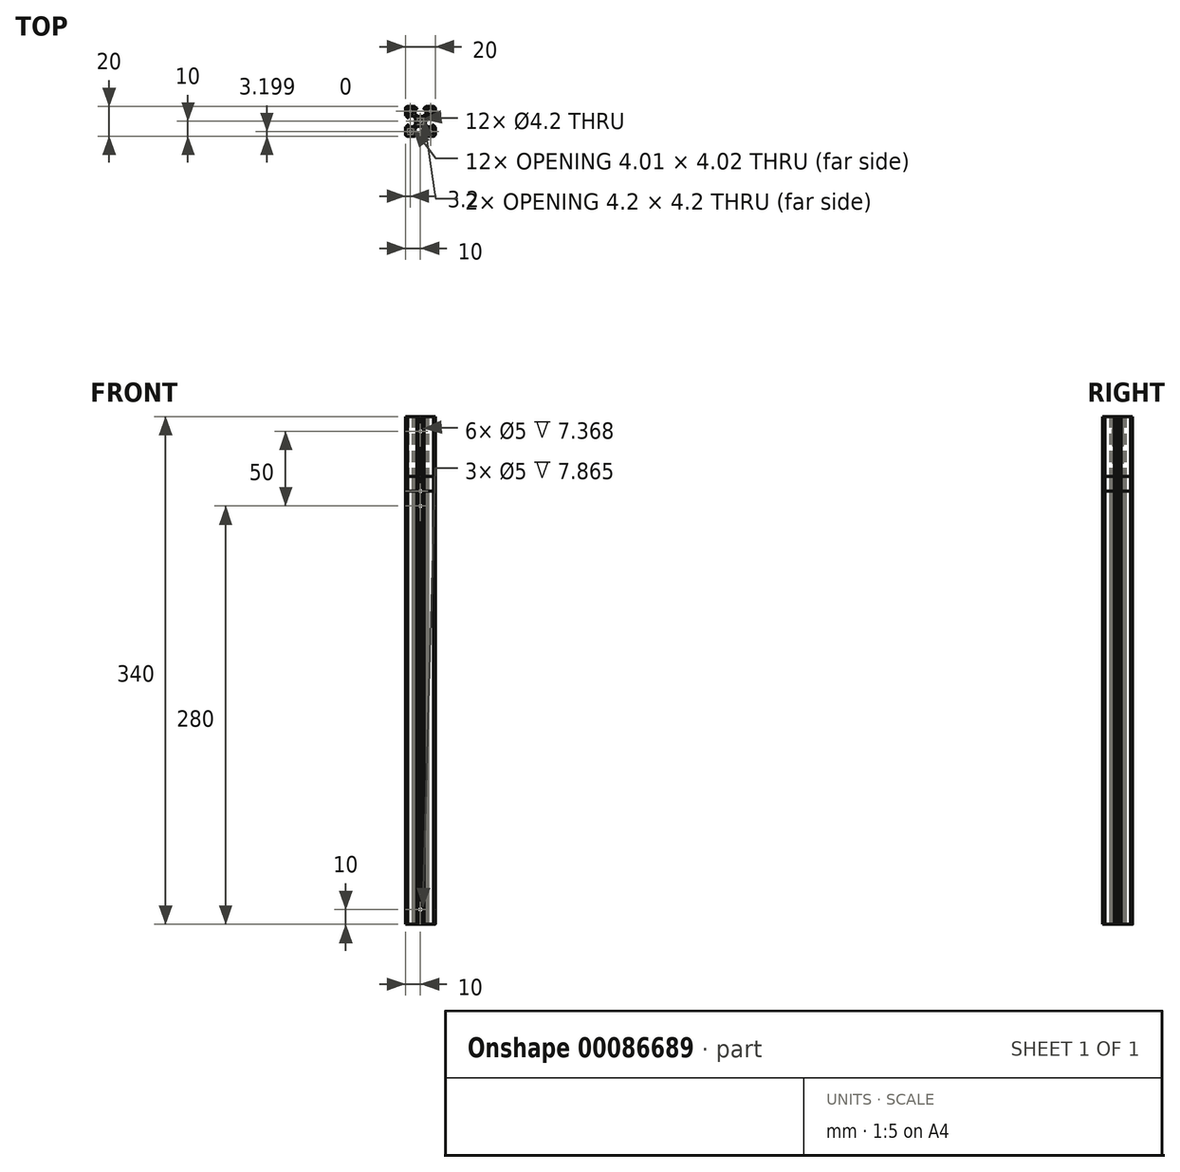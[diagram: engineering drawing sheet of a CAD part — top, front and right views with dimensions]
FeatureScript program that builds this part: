
annotation { "Feature Type Name" : "Feature", "Feature Type Description" : "" }
export const myFeature = defineFeature(function(context is Context, id is Id, definition is map)
    precondition{}
    {
        {
            var Q0;
            Q0=qCreatedBy(makeId("Top.planeOp"),FACE);
            var sketch = newSketch(context, id + "F0", { "sketchPlane" : qUnion([Q0])});
            skCircle(sketch, "E0", {"center": v(0, 0) * mm, "radius": 2.1 * mm});
            skArc(sketch, "E1", {"start": v(-5.39, 4.8) * mm, "mid": v(-4.94, 4.93) * mm, "end": v(-4.8, 5.38) * mm});
            skLineSegment(sketch, "E2", {"start": v(-5.39, 4.8) * mm, "end": v(-8.39, 4.8) * mm});
            skArc(sketch, "E3", {"start": v(-8.8, 5.38) * mm, "mid": v(-8.72, 5) * mm, "end": v(-8.39, 4.8) * mm});
            skLineSegment(sketch, "E4", {"start": v(-8.8, 5.38) * mm, "end": v(-8.8, 8.38) * mm});
            skArc(sketch, "E5", {"start": v(-8.4, 8.8) * mm, "mid": v(-8.67, 8.65) * mm, "end": v(-8.8, 8.38) * mm});
            skLineSegment(sketch, "E6", {"start": v(-8.4, 8.8) * mm, "end": v(-5.4, 8.8) * mm});
            skArc(sketch, "E7", {"start": v(-4.8, 8.38) * mm, "mid": v(-5, 8.72) * mm, "end": v(-5.4, 8.8) * mm});
            skLineSegment(sketch, "E8", {"start": v(-4.8, 8.38) * mm, "end": v(-4.8, 5.38) * mm});
            skArc(sketch, "E9", {"start": v(5.39, -4.8) * mm, "mid": v(4.94, -4.93) * mm, "end": v(4.8, -5.38) * mm});
            skLineSegment(sketch, "E10", {"start": v(5.39, -4.8) * mm, "end": v(8.39, -4.8) * mm});
            skArc(sketch, "E11", {"start": v(8.8, -5.38) * mm, "mid": v(8.72, -5) * mm, "end": v(8.39, -4.8) * mm});
            skLineSegment(sketch, "E12", {"start": v(8.8, -5.38) * mm, "end": v(8.8, -8.38) * mm});
            skArc(sketch, "E13", {"start": v(8.4, -8.8) * mm, "mid": v(8.67, -8.65) * mm, "end": v(8.8, -8.38) * mm});
            skLineSegment(sketch, "E14", {"start": v(8.4, -8.8) * mm, "end": v(5.4, -8.8) * mm});
            skArc(sketch, "E15", {"start": v(4.8, -8.38) * mm, "mid": v(5, -8.72) * mm, "end": v(5.4, -8.8) * mm});
            skLineSegment(sketch, "E16", {"start": v(4.8, -8.38) * mm, "end": v(4.8, -5.38) * mm});
            skLineSegment(sketch, "E17", {"start": v(8.8, 5.38) * mm, "end": v(8.8, 8.38) * mm});
            skArc(sketch, "E18", {"start": v(8.8, 5.38) * mm, "mid": v(8.72, 5) * mm, "end": v(8.39, 4.8) * mm});
            skLineSegment(sketch, "E19", {"start": v(5.39, 4.8) * mm, "end": v(8.39, 4.8) * mm});
            skArc(sketch, "E20", {"start": v(5.39, 4.8) * mm, "mid": v(4.94, 4.93) * mm, "end": v(4.8, 5.38) * mm});
            skLineSegment(sketch, "E21", {"start": v(4.8, 8.38) * mm, "end": v(4.8, 5.38) * mm});
            skArc(sketch, "E22", {"start": v(4.8, 8.38) * mm, "mid": v(5, 8.72) * mm, "end": v(5.4, 8.8) * mm});
            skLineSegment(sketch, "E23", {"start": v(8.4, 8.8) * mm, "end": v(5.4, 8.8) * mm});
            skArc(sketch, "E24", {"start": v(8.4, 8.8) * mm, "mid": v(8.67, 8.65) * mm, "end": v(8.8, 8.38) * mm});
            skLineSegment(sketch, "E25", {"start": v(-8.8, -5.38) * mm, "end": v(-8.8, -8.38) * mm});
            skArc(sketch, "E26", {"start": v(-8.8, -5.38) * mm, "mid": v(-8.72, -5) * mm, "end": v(-8.39, -4.8) * mm});
            skLineSegment(sketch, "E27", {"start": v(-5.39, -4.8) * mm, "end": v(-8.39, -4.8) * mm});
            skArc(sketch, "E28", {"start": v(-5.39, -4.8) * mm, "mid": v(-4.94, -4.93) * mm, "end": v(-4.8, -5.38) * mm});
            skLineSegment(sketch, "E29", {"start": v(-4.8, -8.38) * mm, "end": v(-4.8, -5.38) * mm});
            skArc(sketch, "E30", {"start": v(-4.8, -8.38) * mm, "mid": v(-5, -8.72) * mm, "end": v(-5.4, -8.8) * mm});
            skLineSegment(sketch, "E31", {"start": v(-8.4, -8.8) * mm, "end": v(-5.4, -8.8) * mm});
            skArc(sketch, "E32", {"start": v(-8.4, -8.8) * mm, "mid": v(-8.67, -8.65) * mm, "end": v(-8.8, -8.38) * mm});
            skArc(sketch, "E33", {"start": v(-10, 4.25) * mm, "mid": v(-9.94, 3.95) * mm, "end": v(-9.77, 3.7) * mm});
            skLineSegment(sketch, "E34", {"start": v(-9.77, 3.7) * mm, "end": v(-8.49, 2.4) * mm});
            skArc(sketch, "E35", {"start": v(-8.49, 2.4) * mm, "mid": v(-8.27, 2.36) * mm, "end": v(-8.14, 2.54) * mm});
            skLineSegment(sketch, "E36", {"start": v(-8.14, 2.54) * mm, "end": v(-8.14, 3.6) * mm});
            skLineSegment(sketch, "E37", {"start": v(-8.14, 3.6) * mm, "end": v(-5.03, 3.6) * mm});
            skLineSegment(sketch, "E38", {"start": v(-5.03, 3.6) * mm, "end": v(-3.4, 1.97) * mm});
            skLineSegment(sketch, "E39", {"start": v(-3.4, 1.97) * mm, "end": v(-3.4, 0.38) * mm});
            skLineSegment(sketch, "E40", {"start": v(-3.4, 0.38) * mm, "end": v(-3.02, 0) * mm});
            skLineSegment(sketch, "E41", {"start": v(-3.4, -0.38) * mm, "end": v(-3.02, 0) * mm});
            skLineSegment(sketch, "E42", {"start": v(-3.4, -1.97) * mm, "end": v(-3.4, -0.38) * mm});
            skLineSegment(sketch, "E43", {"start": v(-5.03, -3.6) * mm, "end": v(-3.4, -1.97) * mm});
            skLineSegment(sketch, "E44", {"start": v(-8.14, -3.6) * mm, "end": v(-5.03, -3.6) * mm});
            skLineSegment(sketch, "E45", {"start": v(-8.14, -2.54) * mm, "end": v(-8.14, -3.6) * mm});
            skArc(sketch, "E46", {"start": v(-8.49, -2.4) * mm, "mid": v(-8.27, -2.36) * mm, "end": v(-8.14, -2.54) * mm});
            skLineSegment(sketch, "E47", {"start": v(-9.77, -3.7) * mm, "end": v(-8.49, -2.4) * mm});
            skArc(sketch, "E48", {"start": v(-10, -4.25) * mm, "mid": v(-9.94, -3.95) * mm, "end": v(-9.77, -3.7) * mm});
            skLineSegment(sketch, "E49", {"start": v(-10, -8.58) * mm, "end": v(-10, -4.25) * mm});
            skArc(sketch, "E50", {"start": v(-8.6, -10) * mm, "mid": v(-9.57, -9.56) * mm, "end": v(-10, -8.58) * mm});
            skLineSegment(sketch, "E51", {"start": v(-4.04, -10) * mm, "end": v(-8.6, -10) * mm});
            skArc(sketch, "E52", {"start": v(-3.48, -9.77) * mm, "mid": v(-3.74, -9.94) * mm, "end": v(-4.04, -10) * mm});
            skLineSegment(sketch, "E53", {"start": v(-2.37, -8.66) * mm, "end": v(-3.48, -9.77) * mm});
            skArc(sketch, "E54", {"start": v(-2.55, -8.23) * mm, "mid": v(-2.32, -8.39) * mm, "end": v(-2.37, -8.66) * mm});
            skLineSegment(sketch, "E55", {"start": v(-3.6, -8.23) * mm, "end": v(-2.55, -8.23) * mm});
            skLineSegment(sketch, "E56", {"start": v(-3.6, -5.03) * mm, "end": v(-3.6, -8.23) * mm});
            skLineSegment(sketch, "E57", {"start": v(-2, -3.43) * mm, "end": v(-3.6, -5.03) * mm});
            skLineSegment(sketch, "E58", {"start": v(-0.3, -3.43) * mm, "end": v(-2, -3.43) * mm});
            skLineSegment(sketch, "E59", {"start": v(0, -3.18) * mm, "end": v(-0.3, -3.43) * mm});
            skLineSegment(sketch, "E60", {"start": v(0, -3.18) * mm, "end": v(0.3, -3.43) * mm});
            skLineSegment(sketch, "E61", {"start": v(0.3, -3.43) * mm, "end": v(2, -3.43) * mm});
            skLineSegment(sketch, "E62", {"start": v(2, -3.43) * mm, "end": v(3.6, -5.03) * mm});
            skLineSegment(sketch, "E63", {"start": v(3.6, -5.03) * mm, "end": v(3.6, -8.23) * mm});
            skLineSegment(sketch, "E64", {"start": v(3.6, -8.23) * mm, "end": v(2.55, -8.23) * mm});
            skArc(sketch, "E65", {"start": v(2.55, -8.23) * mm, "mid": v(2.32, -8.39) * mm, "end": v(2.37, -8.66) * mm});
            skLineSegment(sketch, "E66", {"start": v(2.37, -8.66) * mm, "end": v(3.48, -9.77) * mm});
            skArc(sketch, "E67", {"start": v(3.48, -9.77) * mm, "mid": v(3.74, -9.94) * mm, "end": v(4.04, -10) * mm});
            skLineSegment(sketch, "E68", {"start": v(4.04, -10) * mm, "end": v(8.6, -10) * mm});
            skArc(sketch, "E69", {"start": v(8.6, -10) * mm, "mid": v(9.57, -9.56) * mm, "end": v(10, -8.58) * mm});
            skLineSegment(sketch, "E70", {"start": v(10, -8.58) * mm, "end": v(10, -4.25) * mm});
            skArc(sketch, "E71", {"start": v(10, -4.25) * mm, "mid": v(9.94, -3.95) * mm, "end": v(9.77, -3.7) * mm});
            skLineSegment(sketch, "E72", {"start": v(9.77, -3.7) * mm, "end": v(8.49, -2.4) * mm});
            skArc(sketch, "E73", {"start": v(8.49, -2.4) * mm, "mid": v(8.27, -2.36) * mm, "end": v(8.14, -2.54) * mm});
            skLineSegment(sketch, "E74", {"start": v(8.14, -2.54) * mm, "end": v(8.14, -3.6) * mm});
            skLineSegment(sketch, "E75", {"start": v(8.14, -3.6) * mm, "end": v(5.03, -3.6) * mm});
            skLineSegment(sketch, "E76", {"start": v(5.03, -3.6) * mm, "end": v(3.4, -1.97) * mm});
            skLineSegment(sketch, "E77", {"start": v(3.4, -1.97) * mm, "end": v(3.4, -0.38) * mm});
            skLineSegment(sketch, "E78", {"start": v(3.4, -0.38) * mm, "end": v(3.02, 0) * mm});
            skLineSegment(sketch, "E79", {"start": v(3.4, 0.38) * mm, "end": v(3.02, 0) * mm});
            skLineSegment(sketch, "E80", {"start": v(3.4, 1.97) * mm, "end": v(3.4, 0.38) * mm});
            skLineSegment(sketch, "E81", {"start": v(5.03, 3.6) * mm, "end": v(3.4, 1.97) * mm});
            skLineSegment(sketch, "E82", {"start": v(8.14, 3.6) * mm, "end": v(5.03, 3.6) * mm});
            skLineSegment(sketch, "E83", {"start": v(8.14, 2.54) * mm, "end": v(8.14, 3.6) * mm});
            skArc(sketch, "E84", {"start": v(8.49, 2.4) * mm, "mid": v(8.27, 2.36) * mm, "end": v(8.14, 2.54) * mm});
            skLineSegment(sketch, "E85", {"start": v(9.77, 3.7) * mm, "end": v(8.49, 2.4) * mm});
            skArc(sketch, "E86", {"start": v(10, 4.25) * mm, "mid": v(9.94, 3.95) * mm, "end": v(9.77, 3.7) * mm});
            skLineSegment(sketch, "E87", {"start": v(10, 8.58) * mm, "end": v(10, 4.25) * mm});
            skArc(sketch, "E88", {"start": v(8.6, 10) * mm, "mid": v(9.57, 9.56) * mm, "end": v(10, 8.58) * mm});
            skLineSegment(sketch, "E89", {"start": v(4.04, 10) * mm, "end": v(8.6, 10) * mm});
            skArc(sketch, "E90", {"start": v(3.48, 9.77) * mm, "mid": v(3.74, 9.94) * mm, "end": v(4.04, 10) * mm});
            skLineSegment(sketch, "E91", {"start": v(2.37, 8.66) * mm, "end": v(3.48, 9.77) * mm});
            skArc(sketch, "E92", {"start": v(2.55, 8.23) * mm, "mid": v(2.32, 8.39) * mm, "end": v(2.37, 8.66) * mm});
            skLineSegment(sketch, "E93", {"start": v(3.6, 8.23) * mm, "end": v(2.55, 8.23) * mm});
            skLineSegment(sketch, "E94", {"start": v(3.6, 5.03) * mm, "end": v(3.6, 8.23) * mm});
            skLineSegment(sketch, "E95", {"start": v(2, 3.43) * mm, "end": v(3.6, 5.03) * mm});
            skLineSegment(sketch, "E96", {"start": v(0.3, 3.43) * mm, "end": v(2, 3.43) * mm});
            skLineSegment(sketch, "E97", {"start": v(0, 3.18) * mm, "end": v(0.3, 3.43) * mm});
            skLineSegment(sketch, "E98", {"start": v(0, 3.18) * mm, "end": v(-0.3, 3.43) * mm});
            skLineSegment(sketch, "E99", {"start": v(-0.3, 3.43) * mm, "end": v(-2, 3.43) * mm});
            skLineSegment(sketch, "E100", {"start": v(-2, 3.43) * mm, "end": v(-3.6, 5.03) * mm});
            skLineSegment(sketch, "E101", {"start": v(-3.6, 5.03) * mm, "end": v(-3.6, 8.23) * mm});
            skLineSegment(sketch, "E102", {"start": v(-3.6, 8.23) * mm, "end": v(-2.55, 8.23) * mm});
            skArc(sketch, "E103", {"start": v(-2.55, 8.23) * mm, "mid": v(-2.32, 8.39) * mm, "end": v(-2.37, 8.66) * mm});
            skLineSegment(sketch, "E104", {"start": v(-2.37, 8.66) * mm, "end": v(-3.48, 9.77) * mm});
            skArc(sketch, "E105", {"start": v(-3.48, 9.77) * mm, "mid": v(-3.74, 9.94) * mm, "end": v(-4.04, 10) * mm});
            skLineSegment(sketch, "E106", {"start": v(-4.04, 10) * mm, "end": v(-8.6, 10) * mm});
            skArc(sketch, "E107", {"start": v(-8.6, 10) * mm, "mid": v(-9.57, 9.56) * mm, "end": v(-10, 8.58) * mm});
            skLineSegment(sketch, "E108", {"start": v(-10, 8.58) * mm, "end": v(-10, 4.25) * mm});
            skSolve(sketch);
        }
        {
            var Q0;
            Q0=makeQuery(id+"F0.imprint","IMPRINT",FACE,{"disambiguationData":[TD([[makeQuery(id+"F0.imprint","IMPRINT",EDGE,{"derivedFrom":sQuery(id+"F0.wireOp",EDGE,"E0")}),-1.0]])]});
            extrude(context, id + "F1", {"entities" : qUnion([Q0]), "depth" : 290 * mm});
        }
        {
            var Q0;
            Q0=makeQuery(id+"F0.imprint","IMPRINT",FACE,{"disambiguationData":[TD([[makeQuery(id+"F0.imprint","IMPRINT",EDGE,{"derivedFrom":sQuery(id+"F0.wireOp",EDGE,"E0")}),-1.0]])]});
            extrude(context, id + "F2", {"entities" : qUnion([Q0]), "depth" : 300 * mm});
        }
        {
            var Q0;
            Q0=makeQuery(id+"F0.imprint","IMPRINT",FACE,{"disambiguationData":[TD([[makeQuery(id+"F0.imprint","IMPRINT",EDGE,{"derivedFrom":sQuery(id+"F0.wireOp",EDGE,"E0")}),-1.0]])]});
            extrude(context, id + "F3", {"entities" : qUnion([Q0]), "depth" : 340 * mm});
        }
        {
            var Q0;
            Q0=makeQuery(id+"F1.opExtrude","SWEPT_FACE",FACE,{"disambiguationData":[OSD([sQuery(id+"F0.wireOp",EDGE,"E58")])]});
            var sketch = newSketch(context, id + "F4", { "sketchPlane" : qUnion([Q0])});
            skCircle(sketch, "E109", {"center": v(0, 280) * mm, "radius": 2.5 * mm});
            skCircle(sketch, "E110", {"center": v(0, 10) * mm, "radius": 2.5 * mm});
            skSolve(sketch);
        }
        {
            var Q0;
            Q0 = qSketchRegion(id + "F4", true);
            extrude(context, id + "F5", {"entities" : qUnion([Q0]), "operationType" : NewBodyOperationType.REMOVE, "oppositeDirection" : true, "depth" : 25 * mm});
        }
        {
            var Q0;
            Q0=makeQuery(id+"F2.opExtrude","SWEPT_FACE",FACE,{"disambiguationData":[OSD([sQuery(id+"F0.wireOp",EDGE,"E61")])]});
            var sketch = newSketch(context, id + "F6", { "sketchPlane" : qUnion([Q0])});
            skCircle(sketch, "E111", {"center": v(0, 10) * mm, "radius": 2.5 * mm});
            skCircle(sketch, "E112", {"center": v(0, 290) * mm, "radius": 2.5 * mm});
            skSolve(sketch);
        }
        {
            var Q0;
            Q0 = qSketchRegion(id + "F6", true);
            extrude(context, id + "F7", {"entities" : qUnion([Q0]), "operationType" : NewBodyOperationType.REMOVE, "oppositeDirection" : true, "depth" : 25 * mm});
        }
        {
            var Q0;
            Q0=makeQuery(id+"F3.opExtrude","SWEPT_FACE",FACE,{"disambiguationData":[OSD([sQuery(id+"F0.wireOp",EDGE,"E99")])]});
            var sketch = newSketch(context, id + "F8", { "sketchPlane" : qUnion([Q0])});
            skCircle(sketch, "E113", {"center": v(0, 10) * mm, "radius": 2.5 * mm});
            skCircle(sketch, "E114", {"center": v(0, 330) * mm, "radius": 2.5 * mm});
            skSolve(sketch);
        }
        {
            var Q0;
            Q0 = qSketchRegion(id + "F8", true);
            extrude(context, id + "F9", {"entities" : qUnion([Q0]), "operationType" : NewBodyOperationType.REMOVE, "oppositeDirection" : true, "depth" : 25 * mm});
        }
    });
